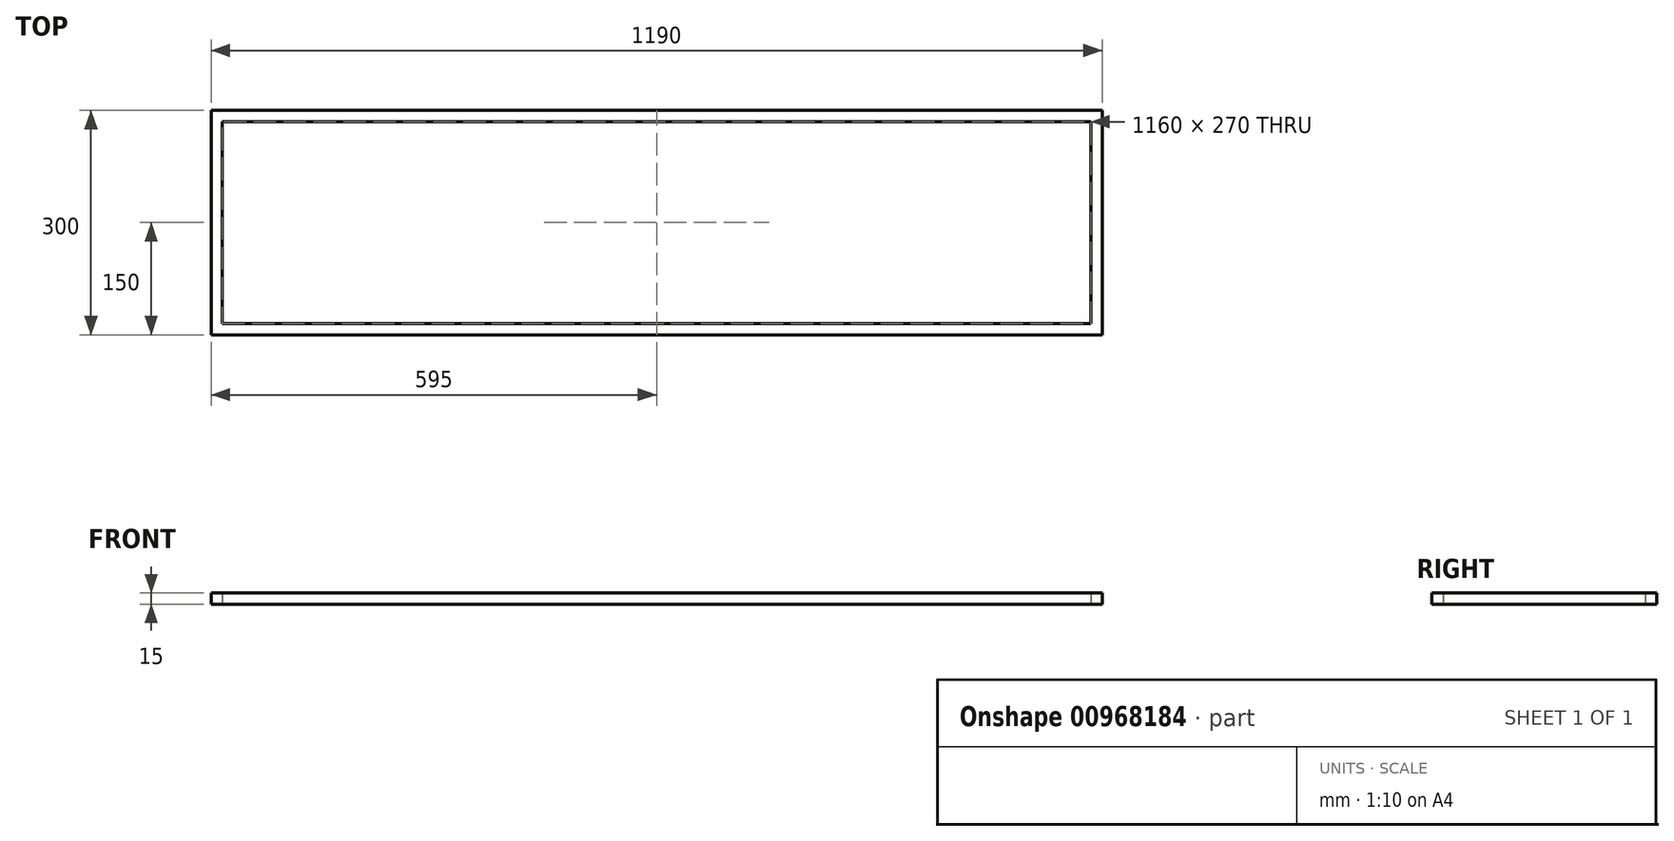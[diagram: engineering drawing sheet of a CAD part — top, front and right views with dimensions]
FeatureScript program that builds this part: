
annotation { "Feature Type Name" : "Feature", "Feature Type Description" : "" }
export const myFeature = defineFeature(function(context is Context, id is Id, definition is map)
    precondition{}
    {
        {
            var Q0;
            Q0=qCreatedBy(makeId("Top.planeOp"),FACE);
            var sketch = newSketch(context, id + "F0", { "sketchPlane" : qUnion([Q0])});
            skLineSegment(sketch, "E0.bottom", {"start": v(0, 0) * mm, "end": v(1190, 0) * mm});
            skLineSegment(sketch, "E0.top", {"start": v(0, 300) * mm, "end": v(1190, 300) * mm});
            skLineSegment(sketch, "E0.left", {"start": v(0, 0) * mm, "end": v(0, 300) * mm});
            skLineSegment(sketch, "E0.right", {"start": v(1190, 0) * mm, "end": v(1190, 300) * mm});
            skLineSegment(sketch, "E1.0", {"start": v(15, 285) * mm, "end": v(1175, 285) * mm});
            skLineSegment(sketch, "E2.0", {"start": v(1175, 15) * mm, "end": v(1175, 285) * mm});
            skLineSegment(sketch, "E3.0", {"start": v(15, 15) * mm, "end": v(1175, 15) * mm});
            skLineSegment(sketch, "E4.0", {"start": v(15, 15) * mm, "end": v(15, 285) * mm});
            skSolve(sketch);
        }
        {
            var Q0;
            Q0=makeQuery(id+"F0.imprint","IMPRINT",FACE,{"disambiguationData":[TD([[makeQuery(id+"F0.imprint","IMPRINT",EDGE,{"derivedFrom":sQuery(id+"F0.wireOp",EDGE,"E0.bottom")}),1.0]])]});
            extrude(context, id + "F1", {"entities" : qUnion([Q0]), "depth" : 15 * mm, "offsetDistance" : 25.4 * mm});
        }
    });
